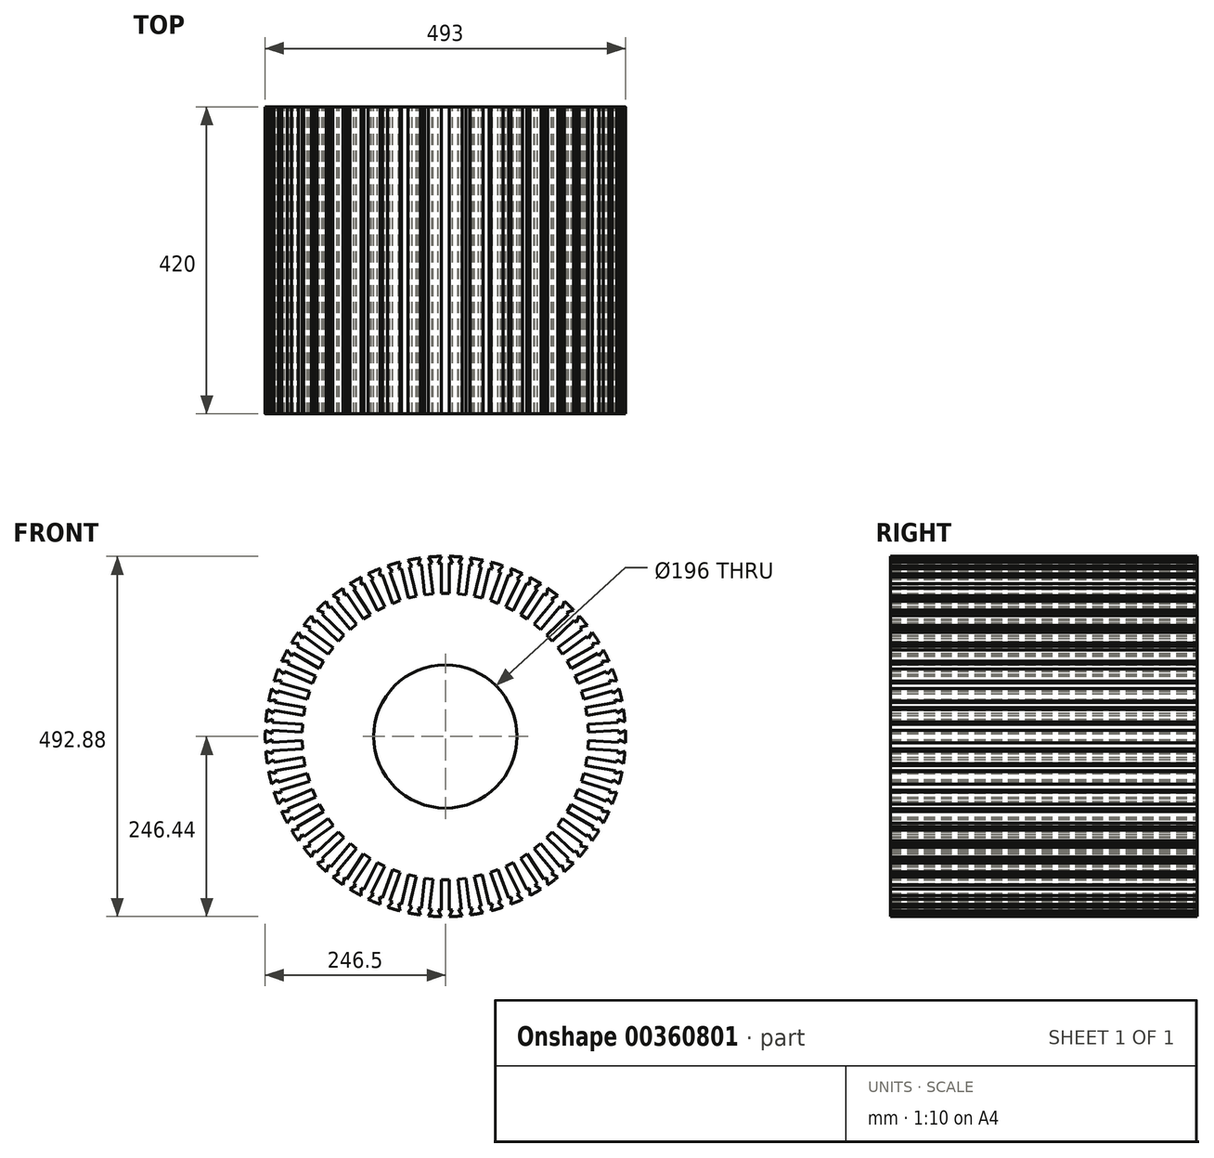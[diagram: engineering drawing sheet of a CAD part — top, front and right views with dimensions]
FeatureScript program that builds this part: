
annotation { "Feature Type Name" : "Feature", "Feature Type Description" : "" }
export const myFeature = defineFeature(function(context is Context, id is Id, definition is map)
    precondition{}
    {
        {
            var Q0;
            Q0=qCreatedBy(makeId("Front.planeOp"),FACE);
            var sketch = newSketch(context, id + "F0", { "sketchPlane" : qUnion([Q0])});
            skArc(sketch, "E0", {"start": v(-5.6, 246.44) * mm, "mid": v(-14.33, 246.08) * mm, "end": v(-23.05, 245.42) * mm});
            skLineSegment(sketch, "E1", {"start": v(0, -271.23) * mm, "end": v(0, 264.46) * mm, "construction": true});
            skLineSegment(sketch, "E2", {"start": v(0, 195.84) * mm, "end": v(-5.6, 195.84) * mm});
            skLineSegment(sketch, "E3", {"start": v(-5.6, 195.84) * mm, "end": v(-5.6, 237.27) * mm});
            skLineSegment(sketch, "E4.MirrorCS", {"start": v(5.6, 195.84) * mm, "end": v(5.6, 237.27) * mm});
            skLineSegment(sketch, "E5.MirrorCS", {"start": v(0, 195.84) * mm, "end": v(5.6, 195.84) * mm});
            skLineSegment(sketch, "E6", {"start": v(-5.6, 237.27) * mm, "end": v(-9.6, 237.27) * mm});
            skLineSegment(sketch, "E7", {"start": v(-9.6, 237.27) * mm, "end": v(-5.6, 246.44) * mm});
            skLineSegment(sketch, "E8.MirrorCS", {"start": v(9.6, 237.27) * mm, "end": v(5.6, 246.44) * mm});
            skLineSegment(sketch, "E9.MirrorCS", {"start": v(5.6, 237.27) * mm, "end": v(9.6, 237.27) * mm});
            skPoint(sketch, "E10.orphan", {"position": v(5.6, 246.44) * mm});
            skLineSegment(sketch, "E11.1.0", {"start": v(28.3, 193.86) * mm, "end": v(33.1, 235.02) * mm});
            skLineSegment(sketch, "E11.1.1", {"start": v(33.1, 235.02) * mm, "end": v(37.08, 234.55) * mm});
            skLineSegment(sketch, "E11.1.2", {"start": v(37.08, 234.55) * mm, "end": v(34.17, 244.12) * mm});
            skLineSegment(sketch, "E11.1.3", {"start": v(22.74, 194.51) * mm, "end": v(28.3, 193.86) * mm});
            skLineSegment(sketch, "E11.1.4", {"start": v(22.74, 194.51) * mm, "end": v(17.17, 195.16) * mm});
            skLineSegment(sketch, "E11.1.5", {"start": v(17.17, 195.16) * mm, "end": v(21.98, 236.32) * mm});
            skLineSegment(sketch, "E11.1.6", {"start": v(21.98, 236.32) * mm, "end": v(18.01, 236.78) * mm});
            skLineSegment(sketch, "E11.1.7", {"start": v(18.01, 236.78) * mm, "end": v(23.05, 245.42) * mm});
            skLineSegment(sketch, "E11.2.0", {"start": v(50.61, 189.27) * mm, "end": v(60.17, 229.58) * mm});
            skLineSegment(sketch, "E11.2.1", {"start": v(60.17, 229.58) * mm, "end": v(64.06, 228.66) * mm});
            skLineSegment(sketch, "E11.2.2", {"start": v(64.06, 228.66) * mm, "end": v(62.28, 238.5) * mm});
            skLineSegment(sketch, "E11.2.3", {"start": v(45.16, 190.56) * mm, "end": v(50.61, 189.27) * mm});
            skLineSegment(sketch, "E11.2.4", {"start": v(45.16, 190.56) * mm, "end": v(39.71, 191.85) * mm});
            skLineSegment(sketch, "E11.2.5", {"start": v(39.71, 191.85) * mm, "end": v(49.27, 232.17) * mm});
            skLineSegment(sketch, "E11.2.6", {"start": v(49.27, 232.17) * mm, "end": v(45.38, 233.09) * mm});
            skLineSegment(sketch, "E11.2.7", {"start": v(45.38, 233.09) * mm, "end": v(51.38, 241.09) * mm});
            skLineSegment(sketch, "E11.3.0", {"start": v(72.24, 182.11) * mm, "end": v(86.41, 221.05) * mm});
            skLineSegment(sketch, "E11.3.1", {"start": v(86.41, 221.05) * mm, "end": v(90.17, 219.68) * mm});
            skLineSegment(sketch, "E11.3.2", {"start": v(90.17, 219.68) * mm, "end": v(89.55, 229.66) * mm});
            skLineSegment(sketch, "E11.3.3", {"start": v(66.98, 184.03) * mm, "end": v(72.24, 182.11) * mm});
            skLineSegment(sketch, "E11.3.4", {"start": v(66.98, 184.03) * mm, "end": v(61.72, 185.94) * mm});
            skLineSegment(sketch, "E11.3.5", {"start": v(61.72, 185.94) * mm, "end": v(75.89, 224.88) * mm});
            skLineSegment(sketch, "E11.3.6", {"start": v(75.89, 224.88) * mm, "end": v(72.13, 226.25) * mm});
            skLineSegment(sketch, "E11.3.7", {"start": v(72.13, 226.25) * mm, "end": v(79.02, 233.49) * mm});
            skLineSegment(sketch, "E11.4.0", {"start": v(92.9, 172.5) * mm, "end": v(111.5, 209.52) * mm});
            skLineSegment(sketch, "E11.4.1", {"start": v(111.5, 209.52) * mm, "end": v(115.07, 207.72) * mm});
            skLineSegment(sketch, "E11.4.2", {"start": v(115.07, 207.72) * mm, "end": v(115.6, 217.71) * mm});
            skLineSegment(sketch, "E11.4.3", {"start": v(87.9, 175) * mm, "end": v(92.9, 172.5) * mm});
            skLineSegment(sketch, "E11.4.4", {"start": v(87.9, 175) * mm, "end": v(82.89, 177.52) * mm});
            skLineSegment(sketch, "E11.4.5", {"start": v(82.89, 177.52) * mm, "end": v(101.48, 214.55) * mm});
            skLineSegment(sketch, "E11.4.6", {"start": v(101.48, 214.55) * mm, "end": v(97.9, 216.34) * mm});
            skLineSegment(sketch, "E11.4.7", {"start": v(97.9, 216.34) * mm, "end": v(105.6, 222.74) * mm});
            skLineSegment(sketch, "E11.5.0", {"start": v(112.3, 160.54) * mm, "end": v(135.06, 195.16) * mm});
            skLineSegment(sketch, "E11.5.1", {"start": v(135.06, 195.16) * mm, "end": v(138.4, 192.96) * mm});
            skLineSegment(sketch, "E11.5.2", {"start": v(138.4, 192.96) * mm, "end": v(140.1, 202.82) * mm});
            skLineSegment(sketch, "E11.5.3", {"start": v(107.61, 163.62) * mm, "end": v(112.3, 160.54) * mm});
            skLineSegment(sketch, "E11.5.4", {"start": v(107.61, 163.62) * mm, "end": v(102.94, 166.7) * mm});
            skLineSegment(sketch, "E11.5.5", {"start": v(102.94, 166.7) * mm, "end": v(125.7, 201.31) * mm});
            skLineSegment(sketch, "E11.5.6", {"start": v(125.7, 201.31) * mm, "end": v(122.36, 203.51) * mm});
            skLineSegment(sketch, "E11.5.7", {"start": v(122.36, 203.51) * mm, "end": v(130.74, 208.97) * mm});
            skLineSegment(sketch, "E11.6.0", {"start": v(130.17, 146.42) * mm, "end": v(156.8, 178.16) * mm});
            skLineSegment(sketch, "E11.6.1", {"start": v(156.8, 178.16) * mm, "end": v(159.87, 175.59) * mm});
            skLineSegment(sketch, "E11.6.2", {"start": v(159.87, 175.59) * mm, "end": v(162.7, 185.18) * mm});
            skLineSegment(sketch, "E11.6.3", {"start": v(125.88, 150.02) * mm, "end": v(130.17, 146.42) * mm});
            skLineSegment(sketch, "E11.6.4", {"start": v(125.88, 150.02) * mm, "end": v(121.6, 153.62) * mm});
            skLineSegment(sketch, "E11.6.5", {"start": v(121.6, 153.62) * mm, "end": v(148.23, 185.36) * mm});
            skLineSegment(sketch, "E11.6.6", {"start": v(148.23, 185.36) * mm, "end": v(145.16, 187.93) * mm});
            skLineSegment(sketch, "E11.6.7", {"start": v(145.16, 187.93) * mm, "end": v(154.12, 192.38) * mm});
            skLineSegment(sketch, "E11.7.0", {"start": v(146.29, 130.32) * mm, "end": v(176.43, 158.75) * mm});
            skLineSegment(sketch, "E11.7.1", {"start": v(176.43, 158.75) * mm, "end": v(179.17, 155.84) * mm});
            skLineSegment(sketch, "E11.7.2", {"start": v(179.17, 155.84) * mm, "end": v(183.1, 165.04) * mm});
            skLineSegment(sketch, "E11.7.3", {"start": v(142.45, 134.4) * mm, "end": v(146.29, 130.32) * mm});
            skLineSegment(sketch, "E11.7.4", {"start": v(142.45, 134.4) * mm, "end": v(138.6, 138.46) * mm});
            skLineSegment(sketch, "E11.7.5", {"start": v(138.6, 138.46) * mm, "end": v(168.74, 166.9) * mm});
            skLineSegment(sketch, "E11.7.6", {"start": v(168.74, 166.9) * mm, "end": v(166, 169.8) * mm});
            skLineSegment(sketch, "E11.7.7", {"start": v(166, 169.8) * mm, "end": v(175.4, 173.19) * mm});
            skLineSegment(sketch, "E11.8.0", {"start": v(160.43, 112.45) * mm, "end": v(193.66, 137.2) * mm});
            skLineSegment(sketch, "E11.8.1", {"start": v(193.66, 137.2) * mm, "end": v(196.05, 133.99) * mm});
            skLineSegment(sketch, "E11.8.2", {"start": v(196.05, 133.99) * mm, "end": v(201.02, 142.67) * mm});
            skLineSegment(sketch, "E11.8.3", {"start": v(157.08, 116.95) * mm, "end": v(160.43, 112.45) * mm});
            skLineSegment(sketch, "E11.8.4", {"start": v(157.08, 116.95) * mm, "end": v(153.74, 121.44) * mm});
            skLineSegment(sketch, "E11.8.5", {"start": v(153.74, 121.44) * mm, "end": v(186.98, 146.18) * mm});
            skLineSegment(sketch, "E11.8.6", {"start": v(186.98, 146.18) * mm, "end": v(184.59, 149.39) * mm});
            skLineSegment(sketch, "E11.8.7", {"start": v(184.59, 149.39) * mm, "end": v(194.33, 151.65) * mm});
            skLineSegment(sketch, "E11.9.0", {"start": v(172.4, 93.07) * mm, "end": v(208.28, 113.79) * mm});
            skLineSegment(sketch, "E11.9.1", {"start": v(208.28, 113.79) * mm, "end": v(210.28, 110.32) * mm});
            skLineSegment(sketch, "E11.9.2", {"start": v(210.28, 110.32) * mm, "end": v(216.22, 118.37) * mm});
            skLineSegment(sketch, "E11.9.3", {"start": v(169.6, 97.92) * mm, "end": v(172.4, 93.07) * mm});
            skLineSegment(sketch, "E11.9.4", {"start": v(169.6, 97.92) * mm, "end": v(166.8, 102.77) * mm});
            skLineSegment(sketch, "E11.9.5", {"start": v(166.8, 102.77) * mm, "end": v(202.68, 123.49) * mm});
            skLineSegment(sketch, "E11.9.6", {"start": v(202.68, 123.49) * mm, "end": v(200.68, 126.95) * mm});
            skLineSegment(sketch, "E11.9.7", {"start": v(200.68, 126.95) * mm, "end": v(210.62, 128.07) * mm});
            skLineSegment(sketch, "E11.10.0", {"start": v(182.04, 72.42) * mm, "end": v(220.08, 88.84) * mm});
            skLineSegment(sketch, "E11.10.1", {"start": v(220.08, 88.84) * mm, "end": v(221.67, 85.16) * mm});
            skLineSegment(sketch, "E11.10.2", {"start": v(221.67, 85.16) * mm, "end": v(228.5, 92.47) * mm});
            skLineSegment(sketch, "E11.10.3", {"start": v(179.82, 77.57) * mm, "end": v(182.04, 72.42) * mm});
            skLineSegment(sketch, "E11.10.4", {"start": v(179.82, 77.57) * mm, "end": v(177.6, 82.7) * mm});
            skLineSegment(sketch, "E11.10.5", {"start": v(177.6, 82.7) * mm, "end": v(215.65, 99.12) * mm});
            skLineSegment(sketch, "E11.10.6", {"start": v(215.65, 99.12) * mm, "end": v(214.06, 102.8) * mm});
            skLineSegment(sketch, "E11.10.7", {"start": v(214.06, 102.8) * mm, "end": v(224.06, 102.75) * mm});
            skLineSegment(sketch, "E11.11.0", {"start": v(189.22, 50.8) * mm, "end": v(228.9, 62.69) * mm});
            skLineSegment(sketch, "E11.11.1", {"start": v(228.9, 62.69) * mm, "end": v(230.06, 58.85) * mm});
            skLineSegment(sketch, "E11.11.2", {"start": v(230.06, 58.85) * mm, "end": v(237.69, 65.31) * mm});
            skLineSegment(sketch, "E11.11.3", {"start": v(187.6, 56.17) * mm, "end": v(189.22, 50.8) * mm});
            skLineSegment(sketch, "E11.11.4", {"start": v(187.6, 56.17) * mm, "end": v(186, 61.53) * mm});
            skLineSegment(sketch, "E11.11.5", {"start": v(186, 61.53) * mm, "end": v(225.7, 73.41) * mm});
            skLineSegment(sketch, "E11.11.6", {"start": v(225.7, 73.41) * mm, "end": v(224.55, 77.25) * mm});
            skLineSegment(sketch, "E11.11.7", {"start": v(224.55, 77.25) * mm, "end": v(234.48, 76.04) * mm});
            skLineSegment(sketch, "E11.12.0", {"start": v(193.83, 28.5) * mm, "end": v(234.64, 35.69) * mm});
            skLineSegment(sketch, "E11.12.1", {"start": v(234.64, 35.69) * mm, "end": v(235.33, 31.75) * mm});
            skLineSegment(sketch, "E11.12.2", {"start": v(235.33, 31.75) * mm, "end": v(243.66, 37.28) * mm});
            skLineSegment(sketch, "E11.12.3", {"start": v(192.86, 34) * mm, "end": v(193.83, 28.5) * mm});
            skLineSegment(sketch, "E11.12.4", {"start": v(192.86, 34) * mm, "end": v(191.89, 39.52) * mm});
            skLineSegment(sketch, "E11.12.5", {"start": v(191.89, 39.52) * mm, "end": v(232.7, 46.72) * mm});
            skLineSegment(sketch, "E11.12.6", {"start": v(232.7, 46.72) * mm, "end": v(232, 50.66) * mm});
            skLineSegment(sketch, "E11.12.7", {"start": v(232, 50.66) * mm, "end": v(241.72, 48.3) * mm});
            skLineSegment(sketch, "E11.13.0", {"start": v(195.83, 5.8) * mm, "end": v(237.2, 8.2) * mm});
            skLineSegment(sketch, "E11.13.1", {"start": v(237.2, 8.2) * mm, "end": v(237.43, 4.21) * mm});
            skLineSegment(sketch, "E11.13.2", {"start": v(237.43, 4.21) * mm, "end": v(246.35, 8.74) * mm});
            skLineSegment(sketch, "E11.13.3", {"start": v(195.5, 11.39) * mm, "end": v(195.83, 5.8) * mm});
            skLineSegment(sketch, "E11.13.4", {"start": v(195.5, 11.39) * mm, "end": v(195.18, 16.98) * mm});
            skLineSegment(sketch, "E11.13.5", {"start": v(195.18, 16.98) * mm, "end": v(236.54, 19.39) * mm});
            skLineSegment(sketch, "E11.13.6", {"start": v(236.54, 19.39) * mm, "end": v(236.31, 23.38) * mm});
            skLineSegment(sketch, "E11.13.7", {"start": v(236.31, 23.38) * mm, "end": v(245.7, 19.92) * mm});
            skLineSegment(sketch, "E11.14.0", {"start": v(195.18, -16.98) * mm, "end": v(236.54, -19.39) * mm});
            skLineSegment(sketch, "E11.14.1", {"start": v(236.54, -19.39) * mm, "end": v(236.31, -23.38) * mm});
            skLineSegment(sketch, "E11.14.2", {"start": v(236.31, -23.38) * mm, "end": v(245.7, -19.92) * mm});
            skLineSegment(sketch, "E11.14.3", {"start": v(195.5, -11.39) * mm, "end": v(195.18, -16.98) * mm});
            skLineSegment(sketch, "E11.14.4", {"start": v(195.5, -11.39) * mm, "end": v(195.83, -5.8) * mm});
            skLineSegment(sketch, "E11.14.5", {"start": v(195.83, -5.8) * mm, "end": v(237.2, -8.2) * mm});
            skLineSegment(sketch, "E11.14.6", {"start": v(237.2, -8.2) * mm, "end": v(237.43, -4.21) * mm});
            skLineSegment(sketch, "E11.14.7", {"start": v(237.43, -4.21) * mm, "end": v(246.35, -8.74) * mm});
            skLineSegment(sketch, "E11.15.0", {"start": v(191.89, -39.52) * mm, "end": v(232.7, -46.72) * mm});
            skLineSegment(sketch, "E11.15.1", {"start": v(232.7, -46.72) * mm, "end": v(232, -50.66) * mm});
            skLineSegment(sketch, "E11.15.2", {"start": v(232, -50.66) * mm, "end": v(241.72, -48.3) * mm});
            skLineSegment(sketch, "E11.15.3", {"start": v(192.86, -34) * mm, "end": v(191.89, -39.52) * mm});
            skLineSegment(sketch, "E11.15.4", {"start": v(192.86, -34) * mm, "end": v(193.83, -28.5) * mm});
            skLineSegment(sketch, "E11.15.5", {"start": v(193.83, -28.5) * mm, "end": v(234.64, -35.69) * mm});
            skLineSegment(sketch, "E11.15.6", {"start": v(234.64, -35.69) * mm, "end": v(235.33, -31.75) * mm});
            skLineSegment(sketch, "E11.15.7", {"start": v(235.33, -31.75) * mm, "end": v(243.66, -37.28) * mm});
            skLineSegment(sketch, "E11.16.0", {"start": v(186, -61.53) * mm, "end": v(225.7, -73.41) * mm});
            skLineSegment(sketch, "E11.16.1", {"start": v(225.7, -73.41) * mm, "end": v(224.55, -77.25) * mm});
            skLineSegment(sketch, "E11.16.2", {"start": v(224.55, -77.25) * mm, "end": v(234.48, -76.04) * mm});
            skLineSegment(sketch, "E11.16.3", {"start": v(187.6, -56.17) * mm, "end": v(186, -61.53) * mm});
            skLineSegment(sketch, "E11.16.4", {"start": v(187.6, -56.17) * mm, "end": v(189.22, -50.8) * mm});
            skLineSegment(sketch, "E11.16.5", {"start": v(189.22, -50.8) * mm, "end": v(228.9, -62.69) * mm});
            skLineSegment(sketch, "E11.16.6", {"start": v(228.9, -62.69) * mm, "end": v(230.06, -58.85) * mm});
            skLineSegment(sketch, "E11.16.7", {"start": v(230.06, -58.85) * mm, "end": v(237.69, -65.31) * mm});
            skLineSegment(sketch, "E11.17.0", {"start": v(177.6, -82.7) * mm, "end": v(215.65, -99.12) * mm});
            skLineSegment(sketch, "E11.17.1", {"start": v(215.65, -99.12) * mm, "end": v(214.06, -102.8) * mm});
            skLineSegment(sketch, "E11.17.2", {"start": v(214.06, -102.8) * mm, "end": v(224.06, -102.75) * mm});
            skLineSegment(sketch, "E11.17.3", {"start": v(179.82, -77.57) * mm, "end": v(177.6, -82.7) * mm});
            skLineSegment(sketch, "E11.17.4", {"start": v(179.82, -77.57) * mm, "end": v(182.04, -72.42) * mm});
            skLineSegment(sketch, "E11.17.5", {"start": v(182.04, -72.42) * mm, "end": v(220.08, -88.84) * mm});
            skLineSegment(sketch, "E11.17.6", {"start": v(220.08, -88.84) * mm, "end": v(221.67, -85.16) * mm});
            skLineSegment(sketch, "E11.17.7", {"start": v(221.67, -85.16) * mm, "end": v(228.5, -92.47) * mm});
            skLineSegment(sketch, "E11.18.0", {"start": v(166.8, -102.77) * mm, "end": v(202.68, -123.49) * mm});
            skLineSegment(sketch, "E11.18.1", {"start": v(202.68, -123.49) * mm, "end": v(200.68, -126.95) * mm});
            skLineSegment(sketch, "E11.18.2", {"start": v(200.68, -126.95) * mm, "end": v(210.62, -128.07) * mm});
            skLineSegment(sketch, "E11.18.3", {"start": v(169.6, -97.92) * mm, "end": v(166.8, -102.77) * mm});
            skLineSegment(sketch, "E11.18.4", {"start": v(169.6, -97.92) * mm, "end": v(172.4, -93.07) * mm});
            skLineSegment(sketch, "E11.18.5", {"start": v(172.4, -93.07) * mm, "end": v(208.28, -113.79) * mm});
            skLineSegment(sketch, "E11.18.6", {"start": v(208.28, -113.79) * mm, "end": v(210.28, -110.32) * mm});
            skLineSegment(sketch, "E11.18.7", {"start": v(210.28, -110.32) * mm, "end": v(216.22, -118.37) * mm});
            skLineSegment(sketch, "E11.19.0", {"start": v(153.74, -121.44) * mm, "end": v(186.98, -146.18) * mm});
            skLineSegment(sketch, "E11.19.1", {"start": v(186.98, -146.18) * mm, "end": v(184.59, -149.39) * mm});
            skLineSegment(sketch, "E11.19.2", {"start": v(184.59, -149.39) * mm, "end": v(194.33, -151.65) * mm});
            skLineSegment(sketch, "E11.19.3", {"start": v(157.08, -116.95) * mm, "end": v(153.74, -121.44) * mm});
            skLineSegment(sketch, "E11.19.4", {"start": v(157.08, -116.95) * mm, "end": v(160.43, -112.45) * mm});
            skLineSegment(sketch, "E11.19.5", {"start": v(160.43, -112.45) * mm, "end": v(193.66, -137.2) * mm});
            skLineSegment(sketch, "E11.19.6", {"start": v(193.66, -137.2) * mm, "end": v(196.05, -133.99) * mm});
            skLineSegment(sketch, "E11.19.7", {"start": v(196.05, -133.99) * mm, "end": v(201.02, -142.67) * mm});
            skLineSegment(sketch, "E11.20.0", {"start": v(138.6, -138.46) * mm, "end": v(168.74, -166.9) * mm});
            skLineSegment(sketch, "E11.20.1", {"start": v(168.74, -166.9) * mm, "end": v(166, -169.8) * mm});
            skLineSegment(sketch, "E11.20.2", {"start": v(166, -169.8) * mm, "end": v(175.4, -173.19) * mm});
            skLineSegment(sketch, "E11.20.3", {"start": v(142.45, -134.4) * mm, "end": v(138.6, -138.46) * mm});
            skLineSegment(sketch, "E11.20.4", {"start": v(142.45, -134.4) * mm, "end": v(146.29, -130.32) * mm});
            skLineSegment(sketch, "E11.20.5", {"start": v(146.29, -130.32) * mm, "end": v(176.43, -158.75) * mm});
            skLineSegment(sketch, "E11.20.6", {"start": v(176.43, -158.75) * mm, "end": v(179.17, -155.84) * mm});
            skLineSegment(sketch, "E11.20.7", {"start": v(179.17, -155.84) * mm, "end": v(183.1, -165.04) * mm});
            skLineSegment(sketch, "E11.21.0", {"start": v(121.6, -153.62) * mm, "end": v(148.23, -185.36) * mm});
            skLineSegment(sketch, "E11.21.1", {"start": v(148.23, -185.36) * mm, "end": v(145.16, -187.93) * mm});
            skLineSegment(sketch, "E11.21.2", {"start": v(145.16, -187.93) * mm, "end": v(154.12, -192.38) * mm});
            skLineSegment(sketch, "E11.21.3", {"start": v(125.88, -150.02) * mm, "end": v(121.6, -153.62) * mm});
            skLineSegment(sketch, "E11.21.4", {"start": v(125.88, -150.02) * mm, "end": v(130.17, -146.42) * mm});
            skLineSegment(sketch, "E11.21.5", {"start": v(130.17, -146.42) * mm, "end": v(156.8, -178.16) * mm});
            skLineSegment(sketch, "E11.21.6", {"start": v(156.8, -178.16) * mm, "end": v(159.87, -175.59) * mm});
            skLineSegment(sketch, "E11.21.7", {"start": v(159.87, -175.59) * mm, "end": v(162.7, -185.18) * mm});
            skLineSegment(sketch, "E11.22.0", {"start": v(102.94, -166.7) * mm, "end": v(125.7, -201.31) * mm});
            skLineSegment(sketch, "E11.22.1", {"start": v(125.7, -201.31) * mm, "end": v(122.36, -203.51) * mm});
            skLineSegment(sketch, "E11.22.2", {"start": v(122.36, -203.51) * mm, "end": v(130.74, -208.97) * mm});
            skLineSegment(sketch, "E11.22.3", {"start": v(107.61, -163.62) * mm, "end": v(102.94, -166.7) * mm});
            skLineSegment(sketch, "E11.22.4", {"start": v(107.61, -163.62) * mm, "end": v(112.3, -160.54) * mm});
            skLineSegment(sketch, "E11.22.5", {"start": v(112.3, -160.54) * mm, "end": v(135.06, -195.16) * mm});
            skLineSegment(sketch, "E11.22.6", {"start": v(135.06, -195.16) * mm, "end": v(138.4, -192.96) * mm});
            skLineSegment(sketch, "E11.22.7", {"start": v(138.4, -192.96) * mm, "end": v(140.1, -202.82) * mm});
            skLineSegment(sketch, "E11.23.0", {"start": v(82.89, -177.52) * mm, "end": v(101.48, -214.55) * mm});
            skLineSegment(sketch, "E11.23.1", {"start": v(101.48, -214.55) * mm, "end": v(97.9, -216.34) * mm});
            skLineSegment(sketch, "E11.23.2", {"start": v(97.9, -216.34) * mm, "end": v(105.6, -222.74) * mm});
            skLineSegment(sketch, "E11.23.3", {"start": v(87.9, -175) * mm, "end": v(82.89, -177.52) * mm});
            skLineSegment(sketch, "E11.23.4", {"start": v(87.9, -175) * mm, "end": v(92.9, -172.5) * mm});
            skLineSegment(sketch, "E11.23.5", {"start": v(92.9, -172.5) * mm, "end": v(111.5, -209.52) * mm});
            skLineSegment(sketch, "E11.23.6", {"start": v(111.5, -209.52) * mm, "end": v(115.07, -207.72) * mm});
            skLineSegment(sketch, "E11.23.7", {"start": v(115.07, -207.72) * mm, "end": v(115.6, -217.71) * mm});
            skLineSegment(sketch, "E11.24.0", {"start": v(61.72, -185.94) * mm, "end": v(75.89, -224.88) * mm});
            skLineSegment(sketch, "E11.24.1", {"start": v(75.89, -224.88) * mm, "end": v(72.13, -226.25) * mm});
            skLineSegment(sketch, "E11.24.2", {"start": v(72.13, -226.25) * mm, "end": v(79.02, -233.49) * mm});
            skLineSegment(sketch, "E11.24.3", {"start": v(66.98, -184.03) * mm, "end": v(61.72, -185.94) * mm});
            skLineSegment(sketch, "E11.24.4", {"start": v(66.98, -184.03) * mm, "end": v(72.24, -182.11) * mm});
            skLineSegment(sketch, "E11.24.5", {"start": v(72.24, -182.11) * mm, "end": v(86.41, -221.05) * mm});
            skLineSegment(sketch, "E11.24.6", {"start": v(86.41, -221.05) * mm, "end": v(90.17, -219.68) * mm});
            skLineSegment(sketch, "E11.24.7", {"start": v(90.17, -219.68) * mm, "end": v(89.55, -229.66) * mm});
            skLineSegment(sketch, "E11.25.0", {"start": v(39.71, -191.85) * mm, "end": v(49.27, -232.17) * mm});
            skLineSegment(sketch, "E11.25.1", {"start": v(49.27, -232.17) * mm, "end": v(45.38, -233.09) * mm});
            skLineSegment(sketch, "E11.25.2", {"start": v(45.38, -233.09) * mm, "end": v(51.38, -241.09) * mm});
            skLineSegment(sketch, "E11.25.3", {"start": v(45.16, -190.56) * mm, "end": v(39.71, -191.85) * mm});
            skLineSegment(sketch, "E11.25.4", {"start": v(45.16, -190.56) * mm, "end": v(50.61, -189.27) * mm});
            skLineSegment(sketch, "E11.25.5", {"start": v(50.61, -189.27) * mm, "end": v(60.17, -229.58) * mm});
            skLineSegment(sketch, "E11.25.6", {"start": v(60.17, -229.58) * mm, "end": v(64.06, -228.66) * mm});
            skLineSegment(sketch, "E11.25.7", {"start": v(64.06, -228.66) * mm, "end": v(62.28, -238.5) * mm});
            skLineSegment(sketch, "E11.26.0", {"start": v(17.17, -195.16) * mm, "end": v(21.98, -236.32) * mm});
            skLineSegment(sketch, "E11.26.1", {"start": v(21.98, -236.32) * mm, "end": v(18.01, -236.78) * mm});
            skLineSegment(sketch, "E11.26.2", {"start": v(18.01, -236.78) * mm, "end": v(23.05, -245.42) * mm});
            skLineSegment(sketch, "E11.26.3", {"start": v(22.74, -194.51) * mm, "end": v(17.17, -195.16) * mm});
            skLineSegment(sketch, "E11.26.4", {"start": v(22.74, -194.51) * mm, "end": v(28.3, -193.86) * mm});
            skLineSegment(sketch, "E11.26.5", {"start": v(28.3, -193.86) * mm, "end": v(33.1, -235.02) * mm});
            skLineSegment(sketch, "E11.26.6", {"start": v(33.1, -235.02) * mm, "end": v(37.08, -234.55) * mm});
            skLineSegment(sketch, "E11.26.7", {"start": v(37.08, -234.55) * mm, "end": v(34.17, -244.12) * mm});
            skLineSegment(sketch, "E11.27.0", {"start": v(-5.6, -195.84) * mm, "end": v(-5.6, -237.27) * mm});
            skLineSegment(sketch, "E11.27.1", {"start": v(-5.6, -237.27) * mm, "end": v(-9.6, -237.27) * mm});
            skLineSegment(sketch, "E11.27.2", {"start": v(-9.6, -237.27) * mm, "end": v(-5.6, -246.44) * mm});
            skLineSegment(sketch, "E11.27.3", {"start": v(0, -195.84) * mm, "end": v(-5.6, -195.84) * mm});
            skLineSegment(sketch, "E11.27.4", {"start": v(0, -195.84) * mm, "end": v(5.6, -195.84) * mm});
            skLineSegment(sketch, "E11.27.5", {"start": v(5.6, -195.84) * mm, "end": v(5.6, -237.27) * mm});
            skLineSegment(sketch, "E11.27.6", {"start": v(5.6, -237.27) * mm, "end": v(9.6, -237.27) * mm});
            skLineSegment(sketch, "E11.27.7", {"start": v(9.6, -237.27) * mm, "end": v(5.6, -246.44) * mm});
            skLineSegment(sketch, "E11.28.0", {"start": v(-28.3, -193.86) * mm, "end": v(-33.1, -235.02) * mm});
            skLineSegment(sketch, "E11.28.1", {"start": v(-33.1, -235.02) * mm, "end": v(-37.08, -234.55) * mm});
            skLineSegment(sketch, "E11.28.2", {"start": v(-37.08, -234.55) * mm, "end": v(-34.17, -244.12) * mm});
            skLineSegment(sketch, "E11.28.3", {"start": v(-22.74, -194.51) * mm, "end": v(-28.3, -193.86) * mm});
            skLineSegment(sketch, "E11.28.4", {"start": v(-22.74, -194.51) * mm, "end": v(-17.17, -195.16) * mm});
            skLineSegment(sketch, "E11.28.5", {"start": v(-17.17, -195.16) * mm, "end": v(-21.98, -236.32) * mm});
            skLineSegment(sketch, "E11.28.6", {"start": v(-21.98, -236.32) * mm, "end": v(-18.01, -236.78) * mm});
            skLineSegment(sketch, "E11.28.7", {"start": v(-18.01, -236.78) * mm, "end": v(-23.05, -245.42) * mm});
            skLineSegment(sketch, "E11.29.0", {"start": v(-50.61, -189.27) * mm, "end": v(-60.17, -229.58) * mm});
            skLineSegment(sketch, "E11.29.1", {"start": v(-60.17, -229.58) * mm, "end": v(-64.06, -228.66) * mm});
            skLineSegment(sketch, "E11.29.2", {"start": v(-64.06, -228.66) * mm, "end": v(-62.28, -238.5) * mm});
            skLineSegment(sketch, "E11.29.3", {"start": v(-45.16, -190.56) * mm, "end": v(-50.61, -189.27) * mm});
            skLineSegment(sketch, "E11.29.4", {"start": v(-45.16, -190.56) * mm, "end": v(-39.71, -191.85) * mm});
            skLineSegment(sketch, "E11.29.5", {"start": v(-39.71, -191.85) * mm, "end": v(-49.27, -232.17) * mm});
            skLineSegment(sketch, "E11.29.6", {"start": v(-49.27, -232.17) * mm, "end": v(-45.38, -233.09) * mm});
            skLineSegment(sketch, "E11.29.7", {"start": v(-45.38, -233.09) * mm, "end": v(-51.38, -241.09) * mm});
            skLineSegment(sketch, "E11.30.0", {"start": v(-72.24, -182.11) * mm, "end": v(-86.41, -221.05) * mm});
            skLineSegment(sketch, "E11.30.1", {"start": v(-86.41, -221.05) * mm, "end": v(-90.17, -219.68) * mm});
            skLineSegment(sketch, "E11.30.2", {"start": v(-90.17, -219.68) * mm, "end": v(-89.55, -229.66) * mm});
            skLineSegment(sketch, "E11.30.3", {"start": v(-66.98, -184.03) * mm, "end": v(-72.24, -182.11) * mm});
            skLineSegment(sketch, "E11.30.4", {"start": v(-66.98, -184.03) * mm, "end": v(-61.72, -185.94) * mm});
            skLineSegment(sketch, "E11.30.5", {"start": v(-61.72, -185.94) * mm, "end": v(-75.89, -224.88) * mm});
            skLineSegment(sketch, "E11.30.6", {"start": v(-75.89, -224.88) * mm, "end": v(-72.13, -226.25) * mm});
            skLineSegment(sketch, "E11.30.7", {"start": v(-72.13, -226.25) * mm, "end": v(-79.02, -233.49) * mm});
            skLineSegment(sketch, "E11.31.0", {"start": v(-92.9, -172.5) * mm, "end": v(-111.5, -209.52) * mm});
            skLineSegment(sketch, "E11.31.1", {"start": v(-111.5, -209.52) * mm, "end": v(-115.07, -207.72) * mm});
            skLineSegment(sketch, "E11.31.2", {"start": v(-115.07, -207.72) * mm, "end": v(-115.6, -217.71) * mm});
            skLineSegment(sketch, "E11.31.3", {"start": v(-87.9, -175) * mm, "end": v(-92.9, -172.5) * mm});
            skLineSegment(sketch, "E11.31.4", {"start": v(-87.9, -175) * mm, "end": v(-82.89, -177.52) * mm});
            skLineSegment(sketch, "E11.31.5", {"start": v(-82.89, -177.52) * mm, "end": v(-101.48, -214.55) * mm});
            skLineSegment(sketch, "E11.31.6", {"start": v(-101.48, -214.55) * mm, "end": v(-97.9, -216.34) * mm});
            skLineSegment(sketch, "E11.31.7", {"start": v(-97.9, -216.34) * mm, "end": v(-105.6, -222.74) * mm});
            skLineSegment(sketch, "E11.32.0", {"start": v(-112.3, -160.54) * mm, "end": v(-135.06, -195.16) * mm});
            skLineSegment(sketch, "E11.32.1", {"start": v(-135.06, -195.16) * mm, "end": v(-138.4, -192.96) * mm});
            skLineSegment(sketch, "E11.32.2", {"start": v(-138.4, -192.96) * mm, "end": v(-140.1, -202.82) * mm});
            skLineSegment(sketch, "E11.32.3", {"start": v(-107.61, -163.62) * mm, "end": v(-112.3, -160.54) * mm});
            skLineSegment(sketch, "E11.32.4", {"start": v(-107.61, -163.62) * mm, "end": v(-102.94, -166.7) * mm});
            skLineSegment(sketch, "E11.32.5", {"start": v(-102.94, -166.7) * mm, "end": v(-125.7, -201.31) * mm});
            skLineSegment(sketch, "E11.32.6", {"start": v(-125.7, -201.31) * mm, "end": v(-122.36, -203.51) * mm});
            skLineSegment(sketch, "E11.32.7", {"start": v(-122.36, -203.51) * mm, "end": v(-130.74, -208.97) * mm});
            skLineSegment(sketch, "E11.33.0", {"start": v(-130.17, -146.42) * mm, "end": v(-156.8, -178.16) * mm});
            skLineSegment(sketch, "E11.33.1", {"start": v(-156.8, -178.16) * mm, "end": v(-159.87, -175.59) * mm});
            skLineSegment(sketch, "E11.33.2", {"start": v(-159.87, -175.59) * mm, "end": v(-162.7, -185.18) * mm});
            skLineSegment(sketch, "E11.33.3", {"start": v(-125.88, -150.02) * mm, "end": v(-130.17, -146.42) * mm});
            skLineSegment(sketch, "E11.33.4", {"start": v(-125.88, -150.02) * mm, "end": v(-121.6, -153.62) * mm});
            skLineSegment(sketch, "E11.33.5", {"start": v(-121.6, -153.62) * mm, "end": v(-148.23, -185.36) * mm});
            skLineSegment(sketch, "E11.33.6", {"start": v(-148.23, -185.36) * mm, "end": v(-145.16, -187.93) * mm});
            skLineSegment(sketch, "E11.33.7", {"start": v(-145.16, -187.93) * mm, "end": v(-154.12, -192.38) * mm});
            skLineSegment(sketch, "E11.34.0", {"start": v(-146.29, -130.32) * mm, "end": v(-176.43, -158.75) * mm});
            skLineSegment(sketch, "E11.34.1", {"start": v(-176.43, -158.75) * mm, "end": v(-179.17, -155.84) * mm});
            skLineSegment(sketch, "E11.34.2", {"start": v(-179.17, -155.84) * mm, "end": v(-183.1, -165.04) * mm});
            skLineSegment(sketch, "E11.34.3", {"start": v(-142.45, -134.4) * mm, "end": v(-146.29, -130.32) * mm});
            skLineSegment(sketch, "E11.34.4", {"start": v(-142.45, -134.4) * mm, "end": v(-138.6, -138.46) * mm});
            skLineSegment(sketch, "E11.34.5", {"start": v(-138.6, -138.46) * mm, "end": v(-168.74, -166.9) * mm});
            skLineSegment(sketch, "E11.34.6", {"start": v(-168.74, -166.9) * mm, "end": v(-166, -169.8) * mm});
            skLineSegment(sketch, "E11.34.7", {"start": v(-166, -169.8) * mm, "end": v(-175.4, -173.19) * mm});
            skLineSegment(sketch, "E11.35.0", {"start": v(-160.43, -112.45) * mm, "end": v(-193.66, -137.2) * mm});
            skLineSegment(sketch, "E11.35.1", {"start": v(-193.66, -137.2) * mm, "end": v(-196.05, -133.99) * mm});
            skLineSegment(sketch, "E11.35.2", {"start": v(-196.05, -133.99) * mm, "end": v(-201.02, -142.67) * mm});
            skLineSegment(sketch, "E11.35.3", {"start": v(-157.08, -116.95) * mm, "end": v(-160.43, -112.45) * mm});
            skLineSegment(sketch, "E11.35.4", {"start": v(-157.08, -116.95) * mm, "end": v(-153.74, -121.44) * mm});
            skLineSegment(sketch, "E11.35.5", {"start": v(-153.74, -121.44) * mm, "end": v(-186.98, -146.18) * mm});
            skLineSegment(sketch, "E11.35.6", {"start": v(-186.98, -146.18) * mm, "end": v(-184.59, -149.39) * mm});
            skLineSegment(sketch, "E11.35.7", {"start": v(-184.59, -149.39) * mm, "end": v(-194.33, -151.65) * mm});
            skLineSegment(sketch, "E11.36.0", {"start": v(-172.4, -93.07) * mm, "end": v(-208.28, -113.79) * mm});
            skLineSegment(sketch, "E11.36.1", {"start": v(-208.28, -113.79) * mm, "end": v(-210.28, -110.32) * mm});
            skLineSegment(sketch, "E11.36.2", {"start": v(-210.28, -110.32) * mm, "end": v(-216.22, -118.37) * mm});
            skLineSegment(sketch, "E11.36.3", {"start": v(-169.6, -97.92) * mm, "end": v(-172.4, -93.07) * mm});
            skLineSegment(sketch, "E11.36.4", {"start": v(-169.6, -97.92) * mm, "end": v(-166.8, -102.77) * mm});
            skLineSegment(sketch, "E11.36.5", {"start": v(-166.8, -102.77) * mm, "end": v(-202.68, -123.49) * mm});
            skLineSegment(sketch, "E11.36.6", {"start": v(-202.68, -123.49) * mm, "end": v(-200.68, -126.95) * mm});
            skLineSegment(sketch, "E11.36.7", {"start": v(-200.68, -126.95) * mm, "end": v(-210.62, -128.07) * mm});
            skLineSegment(sketch, "E11.37.0", {"start": v(-182.04, -72.42) * mm, "end": v(-220.08, -88.84) * mm});
            skLineSegment(sketch, "E11.37.1", {"start": v(-220.08, -88.84) * mm, "end": v(-221.67, -85.16) * mm});
            skLineSegment(sketch, "E11.37.2", {"start": v(-221.67, -85.16) * mm, "end": v(-228.5, -92.47) * mm});
            skLineSegment(sketch, "E11.37.3", {"start": v(-179.82, -77.57) * mm, "end": v(-182.04, -72.42) * mm});
            skLineSegment(sketch, "E11.37.4", {"start": v(-179.82, -77.57) * mm, "end": v(-177.6, -82.7) * mm});
            skLineSegment(sketch, "E11.37.5", {"start": v(-177.6, -82.7) * mm, "end": v(-215.65, -99.12) * mm});
            skLineSegment(sketch, "E11.37.6", {"start": v(-215.65, -99.12) * mm, "end": v(-214.06, -102.8) * mm});
            skLineSegment(sketch, "E11.37.7", {"start": v(-214.06, -102.8) * mm, "end": v(-224.06, -102.75) * mm});
            skLineSegment(sketch, "E11.38.0", {"start": v(-189.22, -50.8) * mm, "end": v(-228.9, -62.69) * mm});
            skLineSegment(sketch, "E11.38.1", {"start": v(-228.9, -62.69) * mm, "end": v(-230.06, -58.85) * mm});
            skLineSegment(sketch, "E11.38.2", {"start": v(-230.06, -58.85) * mm, "end": v(-237.69, -65.31) * mm});
            skLineSegment(sketch, "E11.38.3", {"start": v(-187.6, -56.17) * mm, "end": v(-189.22, -50.8) * mm});
            skLineSegment(sketch, "E11.38.4", {"start": v(-187.6, -56.17) * mm, "end": v(-186, -61.53) * mm});
            skLineSegment(sketch, "E11.38.5", {"start": v(-186, -61.53) * mm, "end": v(-225.7, -73.41) * mm});
            skLineSegment(sketch, "E11.38.6", {"start": v(-225.7, -73.41) * mm, "end": v(-224.55, -77.25) * mm});
            skLineSegment(sketch, "E11.38.7", {"start": v(-224.55, -77.25) * mm, "end": v(-234.48, -76.04) * mm});
            skLineSegment(sketch, "E11.39.0", {"start": v(-193.83, -28.5) * mm, "end": v(-234.64, -35.69) * mm});
            skLineSegment(sketch, "E11.39.1", {"start": v(-234.64, -35.69) * mm, "end": v(-235.33, -31.75) * mm});
            skLineSegment(sketch, "E11.39.2", {"start": v(-235.33, -31.75) * mm, "end": v(-243.66, -37.28) * mm});
            skLineSegment(sketch, "E11.39.3", {"start": v(-192.86, -34) * mm, "end": v(-193.83, -28.5) * mm});
            skLineSegment(sketch, "E11.39.4", {"start": v(-192.86, -34) * mm, "end": v(-191.89, -39.52) * mm});
            skLineSegment(sketch, "E11.39.5", {"start": v(-191.89, -39.52) * mm, "end": v(-232.7, -46.72) * mm});
            skLineSegment(sketch, "E11.39.6", {"start": v(-232.7, -46.72) * mm, "end": v(-232, -50.66) * mm});
            skLineSegment(sketch, "E11.39.7", {"start": v(-232, -50.66) * mm, "end": v(-241.72, -48.3) * mm});
            skLineSegment(sketch, "E11.40.0", {"start": v(-195.83, -5.8) * mm, "end": v(-237.2, -8.2) * mm});
            skLineSegment(sketch, "E11.40.1", {"start": v(-237.2, -8.2) * mm, "end": v(-237.43, -4.21) * mm});
            skLineSegment(sketch, "E11.40.2", {"start": v(-237.43, -4.21) * mm, "end": v(-246.35, -8.74) * mm});
            skLineSegment(sketch, "E11.40.3", {"start": v(-195.5, -11.39) * mm, "end": v(-195.83, -5.8) * mm});
            skLineSegment(sketch, "E11.40.4", {"start": v(-195.5, -11.39) * mm, "end": v(-195.18, -16.98) * mm});
            skLineSegment(sketch, "E11.40.5", {"start": v(-195.18, -16.98) * mm, "end": v(-236.54, -19.39) * mm});
            skLineSegment(sketch, "E11.40.6", {"start": v(-236.54, -19.39) * mm, "end": v(-236.31, -23.38) * mm});
            skLineSegment(sketch, "E11.40.7", {"start": v(-236.31, -23.38) * mm, "end": v(-245.7, -19.92) * mm});
            skLineSegment(sketch, "E11.41.0", {"start": v(-195.18, 16.98) * mm, "end": v(-236.54, 19.39) * mm});
            skLineSegment(sketch, "E11.41.1", {"start": v(-236.54, 19.39) * mm, "end": v(-236.31, 23.38) * mm});
            skLineSegment(sketch, "E11.41.2", {"start": v(-236.31, 23.38) * mm, "end": v(-245.7, 19.92) * mm});
            skLineSegment(sketch, "E11.41.3", {"start": v(-195.5, 11.39) * mm, "end": v(-195.18, 16.98) * mm});
            skLineSegment(sketch, "E11.41.4", {"start": v(-195.5, 11.39) * mm, "end": v(-195.83, 5.8) * mm});
            skLineSegment(sketch, "E11.41.5", {"start": v(-195.83, 5.8) * mm, "end": v(-237.2, 8.2) * mm});
            skLineSegment(sketch, "E11.41.6", {"start": v(-237.2, 8.2) * mm, "end": v(-237.43, 4.21) * mm});
            skLineSegment(sketch, "E11.41.7", {"start": v(-237.43, 4.21) * mm, "end": v(-246.35, 8.74) * mm});
            skLineSegment(sketch, "E11.42.0", {"start": v(-191.89, 39.52) * mm, "end": v(-232.7, 46.72) * mm});
            skLineSegment(sketch, "E11.42.1", {"start": v(-232.7, 46.72) * mm, "end": v(-232, 50.66) * mm});
            skLineSegment(sketch, "E11.42.2", {"start": v(-232, 50.66) * mm, "end": v(-241.72, 48.3) * mm});
            skLineSegment(sketch, "E11.42.3", {"start": v(-192.86, 34) * mm, "end": v(-191.89, 39.52) * mm});
            skLineSegment(sketch, "E11.42.4", {"start": v(-192.86, 34) * mm, "end": v(-193.83, 28.5) * mm});
            skLineSegment(sketch, "E11.42.5", {"start": v(-193.83, 28.5) * mm, "end": v(-234.64, 35.69) * mm});
            skLineSegment(sketch, "E11.42.6", {"start": v(-234.64, 35.69) * mm, "end": v(-235.33, 31.75) * mm});
            skLineSegment(sketch, "E11.42.7", {"start": v(-235.33, 31.75) * mm, "end": v(-243.66, 37.28) * mm});
            skLineSegment(sketch, "E11.43.0", {"start": v(-186, 61.53) * mm, "end": v(-225.7, 73.41) * mm});
            skLineSegment(sketch, "E11.43.1", {"start": v(-225.7, 73.41) * mm, "end": v(-224.55, 77.25) * mm});
            skLineSegment(sketch, "E11.43.2", {"start": v(-224.55, 77.25) * mm, "end": v(-234.48, 76.04) * mm});
            skLineSegment(sketch, "E11.43.3", {"start": v(-187.6, 56.17) * mm, "end": v(-186, 61.53) * mm});
            skLineSegment(sketch, "E11.43.4", {"start": v(-187.6, 56.17) * mm, "end": v(-189.22, 50.8) * mm});
            skLineSegment(sketch, "E11.43.5", {"start": v(-189.22, 50.8) * mm, "end": v(-228.9, 62.69) * mm});
            skLineSegment(sketch, "E11.43.6", {"start": v(-228.9, 62.69) * mm, "end": v(-230.06, 58.85) * mm});
            skLineSegment(sketch, "E11.43.7", {"start": v(-230.06, 58.85) * mm, "end": v(-237.69, 65.31) * mm});
            skLineSegment(sketch, "E11.44.0", {"start": v(-177.6, 82.7) * mm, "end": v(-215.65, 99.12) * mm});
            skLineSegment(sketch, "E11.44.1", {"start": v(-215.65, 99.12) * mm, "end": v(-214.06, 102.8) * mm});
            skLineSegment(sketch, "E11.44.2", {"start": v(-214.06, 102.8) * mm, "end": v(-224.06, 102.75) * mm});
            skLineSegment(sketch, "E11.44.3", {"start": v(-179.82, 77.57) * mm, "end": v(-177.6, 82.7) * mm});
            skLineSegment(sketch, "E11.44.4", {"start": v(-179.82, 77.57) * mm, "end": v(-182.04, 72.42) * mm});
            skLineSegment(sketch, "E11.44.5", {"start": v(-182.04, 72.42) * mm, "end": v(-220.08, 88.84) * mm});
            skLineSegment(sketch, "E11.44.6", {"start": v(-220.08, 88.84) * mm, "end": v(-221.67, 85.16) * mm});
            skLineSegment(sketch, "E11.44.7", {"start": v(-221.67, 85.16) * mm, "end": v(-228.5, 92.47) * mm});
            skLineSegment(sketch, "E11.45.0", {"start": v(-166.8, 102.77) * mm, "end": v(-202.68, 123.49) * mm});
            skLineSegment(sketch, "E11.45.1", {"start": v(-202.68, 123.49) * mm, "end": v(-200.68, 126.95) * mm});
            skLineSegment(sketch, "E11.45.2", {"start": v(-200.68, 126.95) * mm, "end": v(-210.62, 128.07) * mm});
            skLineSegment(sketch, "E11.45.3", {"start": v(-169.6, 97.92) * mm, "end": v(-166.8, 102.77) * mm});
            skLineSegment(sketch, "E11.45.4", {"start": v(-169.6, 97.92) * mm, "end": v(-172.4, 93.07) * mm});
            skLineSegment(sketch, "E11.45.5", {"start": v(-172.4, 93.07) * mm, "end": v(-208.28, 113.79) * mm});
            skLineSegment(sketch, "E11.45.6", {"start": v(-208.28, 113.79) * mm, "end": v(-210.28, 110.32) * mm});
            skLineSegment(sketch, "E11.45.7", {"start": v(-210.28, 110.32) * mm, "end": v(-216.22, 118.37) * mm});
            skLineSegment(sketch, "E11.46.0", {"start": v(-153.74, 121.44) * mm, "end": v(-186.98, 146.18) * mm});
            skLineSegment(sketch, "E11.46.1", {"start": v(-186.98, 146.18) * mm, "end": v(-184.59, 149.39) * mm});
            skLineSegment(sketch, "E11.46.2", {"start": v(-184.59, 149.39) * mm, "end": v(-194.33, 151.65) * mm});
            skLineSegment(sketch, "E11.46.3", {"start": v(-157.08, 116.95) * mm, "end": v(-153.74, 121.44) * mm});
            skLineSegment(sketch, "E11.46.4", {"start": v(-157.08, 116.95) * mm, "end": v(-160.43, 112.45) * mm});
            skLineSegment(sketch, "E11.46.5", {"start": v(-160.43, 112.45) * mm, "end": v(-193.66, 137.2) * mm});
            skLineSegment(sketch, "E11.46.6", {"start": v(-193.66, 137.2) * mm, "end": v(-196.05, 133.99) * mm});
            skLineSegment(sketch, "E11.46.7", {"start": v(-196.05, 133.99) * mm, "end": v(-201.02, 142.67) * mm});
            skLineSegment(sketch, "E11.47.0", {"start": v(-138.6, 138.46) * mm, "end": v(-168.74, 166.9) * mm});
            skLineSegment(sketch, "E11.47.1", {"start": v(-168.74, 166.9) * mm, "end": v(-166, 169.8) * mm});
            skLineSegment(sketch, "E11.47.2", {"start": v(-166, 169.8) * mm, "end": v(-175.4, 173.19) * mm});
            skLineSegment(sketch, "E11.47.3", {"start": v(-142.45, 134.4) * mm, "end": v(-138.6, 138.46) * mm});
            skLineSegment(sketch, "E11.47.4", {"start": v(-142.45, 134.4) * mm, "end": v(-146.29, 130.32) * mm});
            skLineSegment(sketch, "E11.47.5", {"start": v(-146.29, 130.32) * mm, "end": v(-176.43, 158.75) * mm});
            skLineSegment(sketch, "E11.47.6", {"start": v(-176.43, 158.75) * mm, "end": v(-179.17, 155.84) * mm});
            skLineSegment(sketch, "E11.47.7", {"start": v(-179.17, 155.84) * mm, "end": v(-183.1, 165.04) * mm});
            skLineSegment(sketch, "E11.48.0", {"start": v(-121.6, 153.62) * mm, "end": v(-148.23, 185.36) * mm});
            skLineSegment(sketch, "E11.48.1", {"start": v(-148.23, 185.36) * mm, "end": v(-145.16, 187.93) * mm});
            skLineSegment(sketch, "E11.48.2", {"start": v(-145.16, 187.93) * mm, "end": v(-154.12, 192.38) * mm});
            skLineSegment(sketch, "E11.48.3", {"start": v(-125.88, 150.02) * mm, "end": v(-121.6, 153.62) * mm});
            skLineSegment(sketch, "E11.48.4", {"start": v(-125.88, 150.02) * mm, "end": v(-130.17, 146.42) * mm});
            skLineSegment(sketch, "E11.48.5", {"start": v(-130.17, 146.42) * mm, "end": v(-156.8, 178.16) * mm});
            skLineSegment(sketch, "E11.48.6", {"start": v(-156.8, 178.16) * mm, "end": v(-159.87, 175.59) * mm});
            skLineSegment(sketch, "E11.48.7", {"start": v(-159.87, 175.59) * mm, "end": v(-162.7, 185.18) * mm});
            skLineSegment(sketch, "E11.49.0", {"start": v(-102.94, 166.7) * mm, "end": v(-125.7, 201.31) * mm});
            skLineSegment(sketch, "E11.49.1", {"start": v(-125.7, 201.31) * mm, "end": v(-122.36, 203.51) * mm});
            skLineSegment(sketch, "E11.49.2", {"start": v(-122.36, 203.51) * mm, "end": v(-130.74, 208.97) * mm});
            skLineSegment(sketch, "E11.49.3", {"start": v(-107.61, 163.62) * mm, "end": v(-102.94, 166.7) * mm});
            skLineSegment(sketch, "E11.49.4", {"start": v(-107.61, 163.62) * mm, "end": v(-112.3, 160.54) * mm});
            skLineSegment(sketch, "E11.49.5", {"start": v(-112.3, 160.54) * mm, "end": v(-135.06, 195.16) * mm});
            skLineSegment(sketch, "E11.49.6", {"start": v(-135.06, 195.16) * mm, "end": v(-138.4, 192.96) * mm});
            skLineSegment(sketch, "E11.49.7", {"start": v(-138.4, 192.96) * mm, "end": v(-140.1, 202.82) * mm});
            skLineSegment(sketch, "E11.50.0", {"start": v(-82.89, 177.52) * mm, "end": v(-101.48, 214.55) * mm});
            skLineSegment(sketch, "E11.50.1", {"start": v(-101.48, 214.55) * mm, "end": v(-97.9, 216.34) * mm});
            skLineSegment(sketch, "E11.50.2", {"start": v(-97.9, 216.34) * mm, "end": v(-105.6, 222.74) * mm});
            skLineSegment(sketch, "E11.50.3", {"start": v(-87.9, 175) * mm, "end": v(-82.89, 177.52) * mm});
            skLineSegment(sketch, "E11.50.4", {"start": v(-87.9, 175) * mm, "end": v(-92.9, 172.5) * mm});
            skLineSegment(sketch, "E11.50.5", {"start": v(-92.9, 172.5) * mm, "end": v(-111.5, 209.52) * mm});
            skLineSegment(sketch, "E11.50.6", {"start": v(-111.5, 209.52) * mm, "end": v(-115.07, 207.72) * mm});
            skLineSegment(sketch, "E11.50.7", {"start": v(-115.07, 207.72) * mm, "end": v(-115.6, 217.71) * mm});
            skLineSegment(sketch, "E11.51.0", {"start": v(-61.72, 185.94) * mm, "end": v(-75.89, 224.88) * mm});
            skLineSegment(sketch, "E11.51.1", {"start": v(-75.89, 224.88) * mm, "end": v(-72.13, 226.25) * mm});
            skLineSegment(sketch, "E11.51.2", {"start": v(-72.13, 226.25) * mm, "end": v(-79.02, 233.49) * mm});
            skLineSegment(sketch, "E11.51.3", {"start": v(-66.98, 184.03) * mm, "end": v(-61.72, 185.94) * mm});
            skLineSegment(sketch, "E11.51.4", {"start": v(-66.98, 184.03) * mm, "end": v(-72.24, 182.11) * mm});
            skLineSegment(sketch, "E11.51.5", {"start": v(-72.24, 182.11) * mm, "end": v(-86.41, 221.05) * mm});
            skLineSegment(sketch, "E11.51.6", {"start": v(-86.41, 221.05) * mm, "end": v(-90.17, 219.68) * mm});
            skLineSegment(sketch, "E11.51.7", {"start": v(-90.17, 219.68) * mm, "end": v(-89.55, 229.66) * mm});
            skLineSegment(sketch, "E11.52.0", {"start": v(-39.71, 191.85) * mm, "end": v(-49.27, 232.17) * mm});
            skLineSegment(sketch, "E11.52.1", {"start": v(-49.27, 232.17) * mm, "end": v(-45.38, 233.09) * mm});
            skLineSegment(sketch, "E11.52.2", {"start": v(-45.38, 233.09) * mm, "end": v(-51.38, 241.09) * mm});
            skLineSegment(sketch, "E11.52.3", {"start": v(-45.16, 190.56) * mm, "end": v(-39.71, 191.85) * mm});
            skLineSegment(sketch, "E11.52.4", {"start": v(-45.16, 190.56) * mm, "end": v(-50.61, 189.27) * mm});
            skLineSegment(sketch, "E11.52.5", {"start": v(-50.61, 189.27) * mm, "end": v(-60.17, 229.58) * mm});
            skLineSegment(sketch, "E11.52.6", {"start": v(-60.17, 229.58) * mm, "end": v(-64.06, 228.66) * mm});
            skLineSegment(sketch, "E11.52.7", {"start": v(-64.06, 228.66) * mm, "end": v(-62.28, 238.5) * mm});
            skLineSegment(sketch, "E11.53.0", {"start": v(-17.17, 195.16) * mm, "end": v(-21.98, 236.32) * mm});
            skLineSegment(sketch, "E11.53.1", {"start": v(-21.98, 236.32) * mm, "end": v(-18.01, 236.78) * mm});
            skLineSegment(sketch, "E11.53.2", {"start": v(-18.01, 236.78) * mm, "end": v(-23.05, 245.42) * mm});
            skLineSegment(sketch, "E11.53.3", {"start": v(-22.74, 194.51) * mm, "end": v(-17.17, 195.16) * mm});
            skLineSegment(sketch, "E11.53.4", {"start": v(-22.74, 194.51) * mm, "end": v(-28.3, 193.86) * mm});
            skLineSegment(sketch, "E11.53.5", {"start": v(-28.3, 193.86) * mm, "end": v(-33.1, 235.02) * mm});
            skLineSegment(sketch, "E11.53.6", {"start": v(-33.1, 235.02) * mm, "end": v(-37.08, 234.55) * mm});
            skLineSegment(sketch, "E11.53.7", {"start": v(-37.08, 234.55) * mm, "end": v(-34.17, 244.12) * mm});
            skLineSegment(sketch, "E11.anchor1", {"start": v(0, 0) * mm, "end": v(5.6, 195.84) * mm, "construction": true});
            skLineSegment(sketch, "E11.anchor2", {"start": v(0, 0) * mm, "end": v(-17.17, 195.16) * mm, "construction": true});
            skArc(sketch, "E12.trimOffspring", {"start": v(-34.17, 244.12) * mm, "mid": v(-42.8, 242.76) * mm, "end": v(-51.38, 241.09) * mm});
            skArc(sketch, "E13.trimOffspring", {"start": v(-62.28, 238.5) * mm, "mid": v(-70.7, 236.14) * mm, "end": v(-79.02, 233.49) * mm});
            skArc(sketch, "E14.trimOffspring", {"start": v(-89.55, 229.66) * mm, "mid": v(-97.63, 226.34) * mm, "end": v(-105.6, 222.74) * mm});
            skArc(sketch, "E15.trimOffspring", {"start": v(-115.6, 217.71) * mm, "mid": v(-123.25, 213.48) * mm, "end": v(-130.74, 208.97) * mm});
            skArc(sketch, "E16.trimOffspring", {"start": v(-140.1, 202.82) * mm, "mid": v(-147.2, 197.72) * mm, "end": v(-154.12, 192.38) * mm});
            skArc(sketch, "E17.trimOffspring", {"start": v(-162.7, 185.18) * mm, "mid": v(-169.16, 179.3) * mm, "end": v(-175.4, 173.19) * mm});
            skArc(sketch, "E18.trimOffspring", {"start": v(-183.1, 165.04) * mm, "mid": v(-188.83, 158.45) * mm, "end": v(-194.33, 151.65) * mm});
            skArc(sketch, "E19.trimOffspring", {"start": v(-201.02, 142.67) * mm, "mid": v(-205.95, 135.45) * mm, "end": v(-210.62, 128.07) * mm});
            skArc(sketch, "E20.trimOffspring", {"start": v(-216.22, 118.37) * mm, "mid": v(-220.28, 110.63) * mm, "end": v(-224.06, 102.75) * mm});
            skArc(sketch, "E21.trimOffspring", {"start": v(-228.5, 92.47) * mm, "mid": v(-231.63, 84.3) * mm, "end": v(-234.48, 76.04) * mm});
            skArc(sketch, "E22.trimOffspring", {"start": v(-237.69, 65.31) * mm, "mid": v(-239.86, 56.85) * mm, "end": v(-241.72, 48.3) * mm});
            skArc(sketch, "E23.trimOffspring", {"start": v(-243.66, 37.28) * mm, "mid": v(-244.83, 28.62) * mm, "end": v(-245.7, 19.92) * mm});
            skArc(sketch, "E24.trimOffspring", {"start": v(-246.35, 8.74) * mm, "mid": v(-246.5, 0) * mm, "end": v(-246.35, -8.74) * mm});
            skArc(sketch, "E25.trimOffspring", {"start": v(-245.7, -19.92) * mm, "mid": v(-244.83, -28.62) * mm, "end": v(-243.66, -37.28) * mm});
            skArc(sketch, "E26.trimOffspring", {"start": v(-241.72, -48.3) * mm, "mid": v(-239.86, -56.85) * mm, "end": v(-237.69, -65.31) * mm});
            skArc(sketch, "E27.trimOffspring", {"start": v(-234.48, -76.04) * mm, "mid": v(-231.63, -84.3) * mm, "end": v(-228.5, -92.47) * mm});
            skArc(sketch, "E28.trimOffspring", {"start": v(-224.06, -102.75) * mm, "mid": v(-220.28, -110.63) * mm, "end": v(-216.22, -118.37) * mm});
            skArc(sketch, "E29.trimOffspring", {"start": v(-210.62, -128.07) * mm, "mid": v(-205.95, -135.45) * mm, "end": v(-201.02, -142.67) * mm});
            skArc(sketch, "E30.trimOffspring", {"start": v(-194.33, -151.65) * mm, "mid": v(-188.83, -158.45) * mm, "end": v(-183.1, -165.04) * mm});
            skArc(sketch, "E31.trimOffspring", {"start": v(-175.4, -173.19) * mm, "mid": v(-169.16, -179.3) * mm, "end": v(-162.7, -185.18) * mm});
            skArc(sketch, "E32.trimOffspring", {"start": v(-154.12, -192.38) * mm, "mid": v(-147.2, -197.72) * mm, "end": v(-140.1, -202.82) * mm});
            skArc(sketch, "E33.trimOffspring", {"start": v(-130.74, -208.97) * mm, "mid": v(-123.25, -213.48) * mm, "end": v(-115.6, -217.71) * mm});
            skArc(sketch, "E34.trimOffspring", {"start": v(-105.6, -222.74) * mm, "mid": v(-97.63, -226.34) * mm, "end": v(-89.55, -229.66) * mm});
            skArc(sketch, "E35.trimOffspring", {"start": v(-79.02, -233.49) * mm, "mid": v(-70.7, -236.14) * mm, "end": v(-62.28, -238.5) * mm});
            skArc(sketch, "E36.trimOffspring", {"start": v(-51.38, -241.09) * mm, "mid": v(-42.8, -242.76) * mm, "end": v(-34.17, -244.12) * mm});
            skArc(sketch, "E37.trimOffspring", {"start": v(-23.05, -245.42) * mm, "mid": v(-14.33, -246.08) * mm, "end": v(-5.6, -246.44) * mm});
            skArc(sketch, "E38.trimOffspring", {"start": v(5.6, -246.44) * mm, "mid": v(14.33, -246.08) * mm, "end": v(23.05, -245.42) * mm});
            skArc(sketch, "E39.trimOffspring", {"start": v(34.17, -244.12) * mm, "mid": v(42.8, -242.76) * mm, "end": v(51.38, -241.09) * mm});
            skArc(sketch, "E40.trimOffspring", {"start": v(62.28, -238.5) * mm, "mid": v(70.7, -236.14) * mm, "end": v(79.02, -233.49) * mm});
            skArc(sketch, "E41.trimOffspring", {"start": v(89.55, -229.66) * mm, "mid": v(97.63, -226.34) * mm, "end": v(105.6, -222.74) * mm});
            skArc(sketch, "E42.trimOffspring", {"start": v(115.6, -217.71) * mm, "mid": v(123.25, -213.48) * mm, "end": v(130.74, -208.97) * mm});
            skArc(sketch, "E43.trimOffspring", {"start": v(140.1, -202.82) * mm, "mid": v(147.2, -197.72) * mm, "end": v(154.12, -192.38) * mm});
            skArc(sketch, "E44.trimOffspring", {"start": v(162.7, -185.18) * mm, "mid": v(169.16, -179.3) * mm, "end": v(175.4, -173.19) * mm});
            skArc(sketch, "E45.trimOffspring", {"start": v(183.1, -165.04) * mm, "mid": v(188.83, -158.45) * mm, "end": v(194.33, -151.65) * mm});
            skArc(sketch, "E46.trimOffspring", {"start": v(201.02, -142.67) * mm, "mid": v(205.95, -135.45) * mm, "end": v(210.62, -128.07) * mm});
            skArc(sketch, "E47.trimOffspring", {"start": v(216.22, -118.37) * mm, "mid": v(220.28, -110.63) * mm, "end": v(224.06, -102.75) * mm});
            skArc(sketch, "E48.trimOffspring", {"start": v(228.5, -92.47) * mm, "mid": v(231.63, -84.3) * mm, "end": v(234.48, -76.04) * mm});
            skArc(sketch, "E49.trimOffspring", {"start": v(237.69, -65.31) * mm, "mid": v(239.86, -56.85) * mm, "end": v(241.72, -48.3) * mm});
            skArc(sketch, "E50.trimOffspring", {"start": v(243.66, -37.28) * mm, "mid": v(244.83, -28.62) * mm, "end": v(245.7, -19.92) * mm});
            skArc(sketch, "E51.trimOffspring", {"start": v(246.35, -8.74) * mm, "mid": v(246.5, 0) * mm, "end": v(246.35, 8.74) * mm});
            skArc(sketch, "E52.trimOffspring", {"start": v(245.7, 19.92) * mm, "mid": v(244.83, 28.62) * mm, "end": v(243.66, 37.28) * mm});
            skArc(sketch, "E53.trimOffspring", {"start": v(241.72, 48.3) * mm, "mid": v(239.86, 56.85) * mm, "end": v(237.69, 65.31) * mm});
            skArc(sketch, "E54.trimOffspring", {"start": v(234.48, 76.04) * mm, "mid": v(231.63, 84.3) * mm, "end": v(228.5, 92.47) * mm});
            skArc(sketch, "E55.trimOffspring", {"start": v(224.06, 102.75) * mm, "mid": v(220.28, 110.63) * mm, "end": v(216.22, 118.37) * mm});
            skArc(sketch, "E56.trimOffspring", {"start": v(210.62, 128.07) * mm, "mid": v(205.95, 135.45) * mm, "end": v(201.02, 142.67) * mm});
            skArc(sketch, "E57.trimOffspring", {"start": v(194.33, 151.65) * mm, "mid": v(188.83, 158.45) * mm, "end": v(183.1, 165.04) * mm});
            skArc(sketch, "E58.trimOffspring", {"start": v(175.4, 173.19) * mm, "mid": v(169.16, 179.3) * mm, "end": v(162.7, 185.18) * mm});
            skArc(sketch, "E59.trimOffspring", {"start": v(154.12, 192.38) * mm, "mid": v(147.2, 197.72) * mm, "end": v(140.1, 202.82) * mm});
            skArc(sketch, "E60.trimOffspring", {"start": v(130.74, 208.97) * mm, "mid": v(123.25, 213.48) * mm, "end": v(115.6, 217.71) * mm});
            skArc(sketch, "E61.trimOffspring", {"start": v(105.6, 222.74) * mm, "mid": v(97.63, 226.34) * mm, "end": v(89.55, 229.66) * mm});
            skArc(sketch, "E62.trimOffspring", {"start": v(79.02, 233.49) * mm, "mid": v(70.7, 236.14) * mm, "end": v(62.28, 238.5) * mm});
            skArc(sketch, "E63.trimOffspring", {"start": v(51.38, 241.09) * mm, "mid": v(42.8, 242.76) * mm, "end": v(34.17, 244.12) * mm});
            skArc(sketch, "E64.trimOffspring", {"start": v(23.05, 245.42) * mm, "mid": v(14.33, 246.08) * mm, "end": v(5.6, 246.44) * mm});
            skCircle(sketch, "E65", {"center": v(0, 0) * mm, "radius": 98 * mm});
            skSolve(sketch);
        }
        {
            var Q0;
            Q0=qSketchRegion(id+"F0",true);
            extrude(context, id + "F1", {"entities" : qUnion([Q0]), "depth" : 420 * mm});
        }
    });
